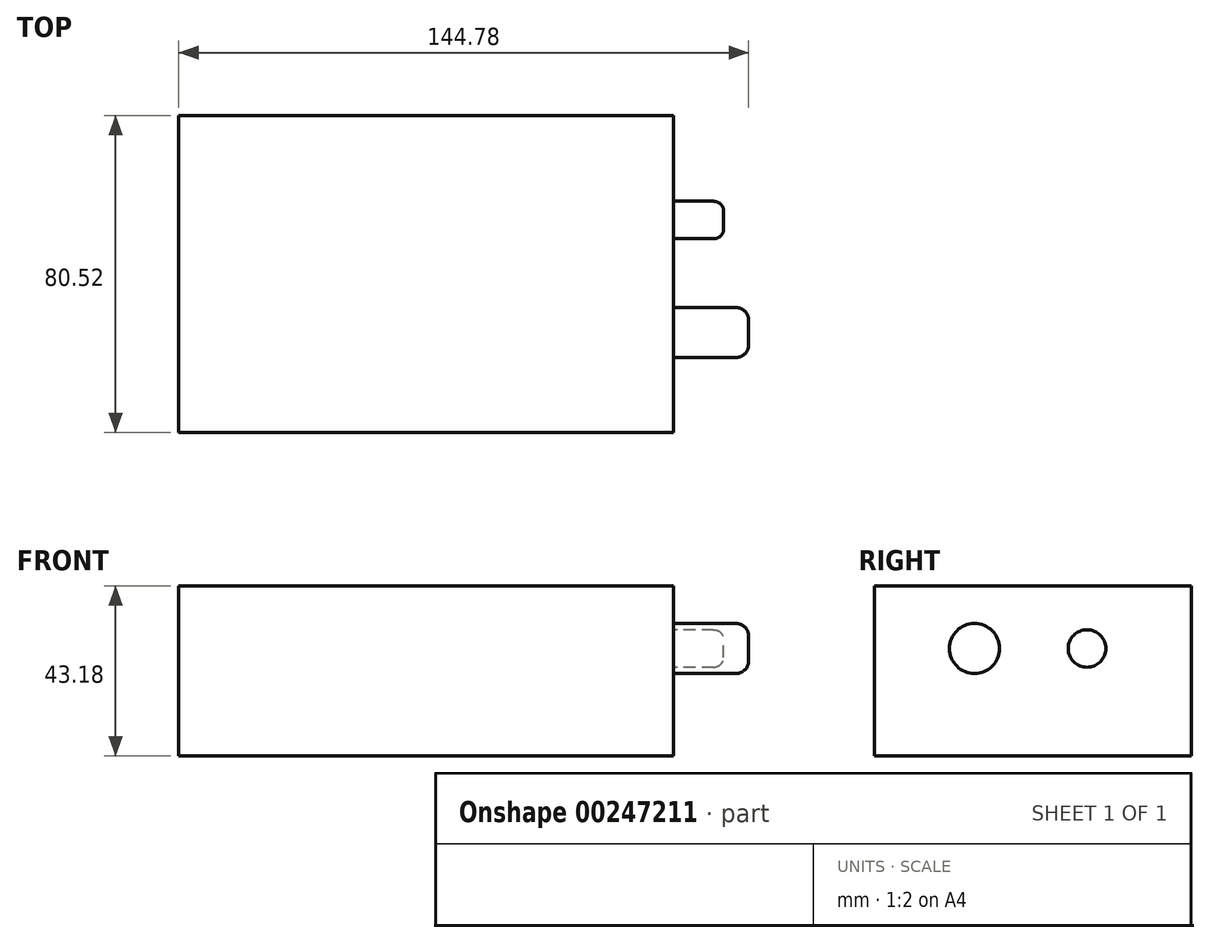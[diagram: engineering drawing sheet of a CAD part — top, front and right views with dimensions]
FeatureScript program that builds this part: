
annotation { "Feature Type Name" : "Feature", "Feature Type Description" : "" }
export const myFeature = defineFeature(function(context is Context, id is Id, definition is map)
    precondition{}
    {
        {
            var Q0;
            Q0=qCreatedBy(makeId("Front.planeOp"),FACE);
            var sketch = newSketch(context, id + "F0", { "sketchPlane" : qUnion([Q0])});
            skLineSegment(sketch, "E0.bottom", {"start": v(0, 0) * mm, "end": v(125.73, 0) * mm});
            skLineSegment(sketch, "E0.top", {"start": v(0, 43.18) * mm, "end": v(125.73, 43.18) * mm});
            skLineSegment(sketch, "E0.left", {"start": v(0, 0) * mm, "end": v(0, 43.18) * mm});
            skLineSegment(sketch, "E0.right", {"start": v(125.73, 0) * mm, "end": v(125.73, 43.18) * mm});
            skSolve(sketch);
        }
        {
            var Q0;
            Q0=makeQuery(id+"F0.imprint","IMPRINT",FACE,{"disambiguationData":[TD([[makeQuery(id+"F0.imprint","IMPRINT",EDGE,{"derivedFrom":sQuery(id+"F0.wireOp",EDGE,"E0.bottom")}),1.0]])]});
            extrude(context, id + "F1", {"entities" : qUnion([Q0]), "depth" : 80.52 * mm});
        }
        {
            var Q0;
            Q0=makeQuery(id+"F1.opExtrude","SWEPT_FACE",FACE,{"disambiguationData":[OSD([sQuery(id+"F0.wireOp",EDGE,"E0.right")])]});
            var sketch = newSketch(context, id + "F2", { "sketchPlane" : qUnion([Q0])});
            skCircle(sketch, "E1", {"center": v(-55.12, 27.3) * mm, "radius": 6.35 * mm});
            skCircle(sketch, "E2", {"center": v(-26.54, 27.3) * mm, "radius": 4.76 * mm});
            skSolve(sketch);
        }
        {
            var Q0;
            Q0=makeQuery(id+"F2.imprint","IMPRINT",FACE,{"disambiguationData":[TD([[makeQuery(id+"F2.imprint","IMPRINT",EDGE,{"derivedFrom":sQuery(id+"F2.wireOp",EDGE,"E1")}),1.0]])]});
            extrude(context, id + "F3", {"entities" : qUnion([Q0]), "operationType" : NewBodyOperationType.ADD, "depth" : 19.05 * mm});
        }
        {
            var Q0;
            Q0=makeQuery(id+"F2.imprint","IMPRINT",FACE,{"disambiguationData":[TD([[makeQuery(id+"F2.imprint","IMPRINT",EDGE,{"derivedFrom":sQuery(id+"F2.wireOp",EDGE,"E2")}),1.0]])]});
            extrude(context, id + "F4", {"entities" : qUnion([Q0]), "operationType" : NewBodyOperationType.ADD, "depth" : 12.7 * mm});
        }
        {
            var Q0;
            Q0=makeQuery(id+"F3.opExtrude","CAP_EDGE",EDGE,{"disambiguationData":[OSD([sQuery(id+"F2.wireOp",EDGE,"E1")])],"isStart":false});
            fillet(context, id + "F5", {"entities" : qUnion([Q0]), "radius" : 3.17 * mm, "tangentPropagation" : true, "allowEdgeOverflow" : false});
        }
        {
            var Q0;
            Q0=makeQuery(id+"F4.opExtrude","CAP_EDGE",EDGE,{"disambiguationData":[OSD([sQuery(id+"F2.wireOp",EDGE,"E2")])],"isStart":false});
            fillet(context, id + "F6", {"entities" : qUnion([Q0]), "radius" : 2.54 * mm, "tangentPropagation" : true, "allowEdgeOverflow" : false});
        }
    });
